# Revit family: ВентКлиматСтрой Вентилятор подпора крышный осевой ВКОп
name_source: partatom
category: Оборудование
units: mm (PartAtom-declared; Revit-internal decimal feet)

## family parameters
Всегда вертикально = Да
Заголовок OmniClass = Fans for Air Ductwork
На основе рабочей плоскости = Нет
Номер OmniClass = 23.75.35.17.11
Общий = Нет
При загрузке вырезать с полостями = Нет
Размер круглого соединителя = Использовать диаметр
Тип детали = Нормальный
Точка расчета площади = Да

## types (23) — shared parameters
ADSK_Версия Revit = 2019
ADSK_Версия семейства = rev.1
ADSK_Единица измерения = шт.
ADSK_Классификация нагрузок = Прочее
ADSK_Количество = 1
ADSK_Количество фаз числовое = 3
ADSK_Напряжение = 380 В
ADSK_Предел огнестойкости = 120
ADSK_Предел огнестойкости экземпляра = 120 мин.
Data = ВКОп-13-284
Poles = 3
Описание = Вентилятор осевой крышный для систем подпора при пожаре
УГО_3D = Да
УшкоШирина = 60 мм
zero-valued in all types: ADSK_Материал тип подсчета

## per-type parameters (varying)
| type | D | D2 | D4 | H | H2 | R1 | R2 | Re | STM_A | STM_B | STM_C | W1 | W1' | W2 | W2' | f | h | МинРазмерШахты | Полюсов |
| ВКОп 13-284-12К-4 (4 полюсный) | 400 мм | 548 мм | 750 мм | 705 мм | 388 мм | 215 мм | 230 мм | 201 мм | 565 мм | 730 мм | 465 мм | 695 мм | 495 мм | 956 мм | 756 мм | 30 мм | 440 мм | 545 мм | 4 |
| ВКОп 13-284-12К-4 (2 полюсный) | 400 мм | 548 мм | 750 мм | 705 мм | 388 мм | 215 мм | 230 мм | 201 мм | 565 мм | 730 мм | 465 мм | 695 мм | 495 мм | 956 мм | 756 мм | 30 мм | 440 мм | 545 мм | 2 |
| ВКОп 13-284-12К-4,5 (4 полюсный) | 450 мм | 655 мм | 935 мм | 740 мм | 407 мм | 255 мм | 275 мм | 226 мм | 615 мм | 780 мм | 515 мм | 860 мм | 660 мм | 1014 мм | 814 мм | 50 мм | 440 мм | 595 мм | 4 |
| ВКОп 13-284-12К-4,5 (2 полюсный) | 450 мм | 655 мм | 935 мм | 740 мм | 407 мм | 255 мм | 275 мм | 226 мм | 615 мм | 780 мм | 515 мм | 860 мм | 660 мм | 1014 мм | 814 мм | 50 мм | 440 мм | 595 мм | 2 |
| ВКОп 13-284-12К-5 (4 полюсный) | 500 мм | 680 мм | 935 мм | 840 мм | 462 мм | 265 мм | 280 мм | 251 мм | 665 мм | 830 мм | 565 мм | 860 мм | 660 мм | 1072 мм | 872 мм | 30 мм | 510 мм | 645 мм | 4 |
| ВКОп 13-284-12К-5 (2 полюсный) | 500 мм | 680 мм | 935 мм | 840 мм | 462 мм | 265 мм | 280 мм | 251 мм | 665 мм | 830 мм | 565 мм | 860 мм | 660 мм | 1072 мм | 872 мм | 30 мм | 510 мм | 645 мм | 2 |
| ВКОп 13-284-12К-5,6 (4 полюсный) | 560 мм | 820 мм | 1170 мм | 985 мм | 542 мм | 310 мм | 330 мм | 281 мм | 725 мм | 890 мм | 625 мм | 1080 мм | 880 мм | 1141 мм | 941 мм | 50 мм | 625 мм | 705 мм | 4 |
| ВКОп 13-284-12К-5,6 (2 полюсный) | 560 мм | 820 мм | 1170 мм | 985 мм | 542 мм | 310 мм | 330 мм | 281 мм | 725 мм | 890 мм | 625 мм | 1080 мм | 880 мм | 1141 мм | 941 мм | 50 мм | 625 мм | 705 мм | 2 |
| ВКОп 13-284-12К-6,3 (4 полюсный) | 630 мм | 855 мм | 1170 мм | 985 мм | 542 мм | 345 мм | 365 мм | 316 мм | 790 мм | 960 мм | 695 мм | 1080 мм | 880 мм | 1222 мм | 1022 мм | 50 мм | 625 мм | 775 мм | 4 |
| ВКОп 13-284-12К-6,3 (2 полюсный) | 630 мм | 855 мм | 1170 мм | 985 мм | 542 мм | 345 мм | 365 мм | 316 мм | 790 мм | 960 мм | 695 мм | 1080 мм | 880 мм | 1222 мм | 1022 мм | 50 мм | 625 мм | 775 мм | 2 |
| ВКОп 13-284-12К-7,1 (4 полюсный) | 710 мм | 965 мм | 1321 мм | 1038 мм | 571 мм | 385 мм | 405 мм | 356 мм | 875 мм | 1040 мм | 775 мм | 1220 мм | 1020 мм | 1314 мм | 1114 мм | 50 мм | 625 мм | 855 мм | 4 |
| ВКОп 13-284-12К-7,1 (2 полюсный) | 710 мм | 965 мм | 1321 мм | 1038 мм | 571 мм | 385 мм | 405 мм | 356 мм | 875 мм | 1040 мм | 775 мм | 1220 мм | 1020 мм | 1314 мм | 1114 мм | 50 мм | 625 мм | 855 мм | 2 |
| ВКОп 13-284-12К-8 (6 полюсный) | 800 мм | 1148 мм | 1617 мм | 1145 мм | 630 мм | 430 мм | 450 мм | 401 мм | 1050 мм | 1210 мм | 865 мм | 1495 мм | 1295 мм | 1430 мм | 1230 мм | 50 мм | 625 мм | 945 мм | 6 |
| ВКОп 13-284-12К-8 (4 полюсный) | 800 мм | 1148 мм | 1617 мм | 1145 мм | 630 мм | 430 мм | 450 мм | 401 мм | 1050 мм | 1210 мм | 865 мм | 1495 мм | 1295 мм | 1430 мм | 1230 мм | 50 мм | 625 мм | 945 мм | 4 |
| ВКОп 13-284-12К-8 (2 полюсный) | 800 мм | 1148 мм | 1617 мм | 1145 мм | 630 мм | 430 мм | 450 мм | 401 мм | 1050 мм | 1210 мм | 865 мм | 1495 мм | 1295 мм | 1430 мм | 1230 мм | 50 мм | 625 мм | 945 мм | 2 |
| ВКОп 13-284-12К-9 (6 полюсный) | 900 мм | 1198 мм | 1617 мм | 1335 мм | 734 мм | 480 мм | 500 мм | 451 мм | 1090 мм | 1230 мм | 965 мм | 1495 мм | 1295 мм | 1616 мм | 1416 мм | 50 мм | 815 мм | 1045 мм | 6 |
| ВКОп 13-284-12К-9 (4 полюсный) | 900 мм | 1198 мм | 1617 мм | 1335 мм | 734 мм | 480 мм | 500 мм | 451 мм | 1090 мм | 1230 мм | 965 мм | 1495 мм | 1295 мм | 1616 мм | 1416 мм | 50 мм | 815 мм | 1045 мм | 4 |
| ВКОп 13-284-12К-10 (6 полюсный) | 1000 мм | 1433 мм | 2017 мм | 1470 мм | 809 мм | 535 мм | 555 мм | 501 мм | 1260 мм | 1420 мм | 1065 мм | 1865 мм | 1665 мм | 1724 мм | 1524 мм | 55 мм | 815 мм | 1145 мм | 6 |
| ВКОп 13-284-12К-10 (4 полюсный) | 1000 мм | 1433 мм | 2017 мм | 1470 мм | 809 мм | 535 мм | 555 мм | 501 мм | 1260 мм | 1420 мм | 1065 мм | 1865 мм | 1665 мм | 1724 мм | 1524 мм | 55 мм | 815 мм | 1145 мм | 4 |
| ВКОп 13-284-12К-11,2 (6 полюсный) | 1120 мм | 1493 мм | 2017 мм | 1605 мм | 883 мм | 598 мм | 618 мм | 561 мм | 1390 мм | 1450 мм | 1185 мм | 1865 мм | 1665 мм | 1875 мм | 1675 мм | 58 мм | 950 мм | 1265 мм | 6 |
| ВКОп 13-284-12К-11,2 (4 полюсный) | 1120 мм | 1493 мм | 2017 мм | 1605 мм | 883 мм | 598 мм | 618 мм | 561 мм | 1390 мм | 1450 мм | 1185 мм | 1865 мм | 1665 мм | 1875 мм | 1675 мм | 58 мм | 950 мм | 1265 мм | 4 |
| ВКОп 13-284-12К-12,5 (8 полюсный) | 1250 мм | 1665 мм | 2255 мм | 1945 мм | 1070 мм | 660 мм | 680 мм | 626 мм | 1545 мм | 1700 мм | 1360 мм | 2080 мм | 1880 мм | 2018 мм | 1818 мм | 55 мм | 1250 мм | 1395 мм | 8 |
| ВКОп 13-284-12К-12,5 (6 полюсный) | 1250 мм | 1665 мм | 2255 мм | 1945 мм | 1070 мм | 660 мм | 680 мм | 626 мм | 1545 мм | 1700 мм | 1360 мм | 2080 мм | 1880 мм | 2018 мм | 1818 мм | 55 мм | 1250 мм | 1395 мм | 6 |

## geometry (parser evidence)
native form markers: Blend x2, Sweep x3
no freeform markers — native parametric forms only
